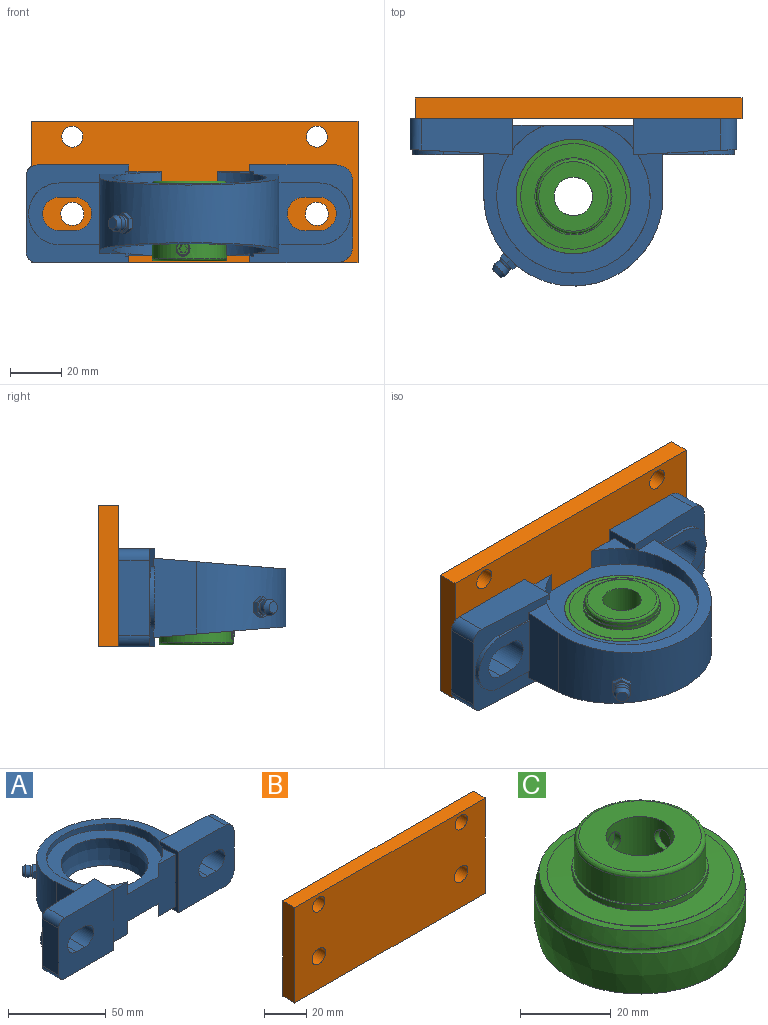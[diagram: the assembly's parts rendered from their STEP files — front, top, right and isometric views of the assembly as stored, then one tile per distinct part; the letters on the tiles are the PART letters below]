
ASSEMBLY  parts=3 mates=2
PART A: 64 faces, bbox 127x65x38 mm
  f0: plane 47x32.59mm, normal (0,-1,0), area 1189.2mm2, adj f1,f23,f24,f27,f29,f30,f32,f33
  f1: plane 38x14mm, normal (-1,0,0), area 163.5mm2, adj f0,f7,f24,f25,f29,f34,f35,f48
  f2: cylinder r=34.8mm len=69.6mm, axis (0,0,-1), area 2648.8mm2, adj f3,f4,f22,f28,f55
  f3: plane 30.82x16.77mm, normal (1,0,0), area 480.2mm2, adj f2,f8,f11,f12,f22,f25,f28
  f4: plane 30.82x16.77mm, normal (-1,0,0), area 480.2mm2, adj f2,f15,f18,f19,f22,f26,f28
  f5: plane 35.67x14mm, normal (0,0,1), area 467.5mm2, adj f26,f27,f47,f54
  f6: plane 35.67x14mm, normal (0,0,-1), area 467.5mm2, adj f26,f27,f47,f51
  f7: plane 33.5x14mm, normal (0,0,-1), area 440.9mm2, adj f1,f25,f50,f52
  f8: plane 15.7x1.35mm, normal (0,0,-1), area 15mm2, adj f3,f12,f25,f63
  f9: plane 14x6mm, normal (0,0,-1), area 84mm2, adj f10,f12,f14,f50
  f10: cylinder r=6.5mm len=14mm, axis (0,-1,0), area 285.9mm2, adj f9,f12,f13,f50
  f11: plane 15.7x1.35mm, normal (0,0,1), area 15mm2, adj f3,f12,f25,f63
  f12: plane 27.7x24mm, normal (0,1,0), area 392.3mm2, adj f3,f8,f9,f10,f11,f13,f14,f63
  f13: plane 14x6mm, normal (0,0,1), area 84mm2, adj f10,f12,f14,f50
  f14: cylinder r=6.5mm len=14mm, axis (0,-1,0), area 285.9mm2, adj f9,f12,f13,f50
  f15: plane 15.7x1.35mm, normal (0,0,1), area 15mm2, adj f4,f19,f26,f62
  f16: plane 14x6mm, normal (0,0,-1), area 84mm2, adj f17,f19,f21,f47
  f17: cylinder r=6.5mm len=14mm, axis (0,-1,0), area 285.9mm2, adj f16,f19,f20,f47
  f18: plane 15.7x1.35mm, normal (0,0,-1), area 15mm2, adj f4,f19,f26,f62
  f19: plane 27.7x24mm, normal (0,1,0), area 392.3mm2, adj f4,f15,f16,f17,f18,f20,f21,f62
  f20: plane 14x6mm, normal (0,0,1), area 84mm2, adj f17,f19,f21,f47
  f21: cylinder r=6.5mm len=14mm, axis (0,-1,0), area 285.9mm2, adj f16,f19,f20,f47
  f22: plane 69.6x54.55mm, normal (0,0.08,1), area 728.5mm2, adj f2,f3,f4,f25,f26,f61
  f23: plane 13.31x10.18mm, normal (0,0.08,1), area 47.9mm2, adj f0,f27,f61
  f24: plane 13.31x10.18mm, normal (0,0.08,1), area 47.9mm2, adj f0,f1,f61
  f25: plane 40x38mm, normal (0.05,1,0), area 548.5mm2, adj f1,f3,f7,f8,f11,f22,f28,f34
  f26: plane 40x38mm, normal (-0.05,1,0), area 558.1mm2, adj f4,f5,f6,f15,f18,f22,f27,f28
  f27: plane 38x14mm, normal (1,0,0), area 163.5mm2, adj f0,f5,f6,f23,f26,f30,f31,f36
  f28: plane 69.6x54.55mm, normal (0,0.08,-1), area 726.9mm2, adj f2,f3,f4,f25,f26,f60
  f29: plane 13.31x10.18mm, normal (0,0.08,-1), area 47.9mm2, adj f0,f1,f60
  f30: plane 13.31x10.18mm, normal (0,0.08,-1), area 47.9mm2, adj f0,f27,f60
  f31: plane 2.12x1.46mm, normal (0,0,-1), area 1.6mm2, adj f26,f27,f61
  f32: plane 59.6x57.5mm, normal (0,0,1), area 1200.7mm2, adj f0,f59,f61
  f33: plane 59.6x57.5mm, normal (0,0,-1), area 1200.7mm2, adj f0,f59,f60
  f34: plane 2.12x1.46mm, normal (0,0,1), area 1.6mm2, adj f1,f25,f60
  f35: plane 2.12x1.46mm, normal (0,0,-1), area 1.6mm2, adj f1,f25,f61
  f36: plane 2.12x1.46mm, normal (0,0,1), area 1.6mm2, adj f26,f27,f60
  f37: plane 4.5x3.18mm, normal (-0.71,0.71,0), area 15.9mm2, adj f58
  f38: plane 8.08x4.95mm, normal (-0.71,0.71,0), area 14.2mm2, adj f40,f41,f42,f43,f44,f45,f56
  f39: plane 8.08x4.95mm, normal (0.71,-0.71,0), area 14.2mm2, adj f40,f41,f42,f43,f44,f45,f55
  f40: plane 3.89x3.89mm, normal (-0.35,-0.35,0.87), area 8.1mm2, adj f38,f39,f41,f45
  f41: plane 4.04x1.41mm, normal (-0.71,-0.71,0), area 8.1mm2, adj f38,f39,f40,f42
  f42: plane 3.89x3.89mm, normal (-0.35,-0.35,-0.87), area 8.1mm2, adj f38,f39,f41,f43
  f43: plane 3.89x3.89mm, normal (0.35,0.35,-0.87), area 8.1mm2, adj f38,f39,f42,f44
  f44: plane 4.04x1.41mm, normal (0.71,0.71,0), area 8.1mm2, adj f38,f39,f43,f45
  f45: plane 3.89x3.89mm, normal (0.35,0.35,0.87), area 8.1mm2, adj f38,f39,f40,f44
  f46: plane 29.33x12mm, normal (-1,0,0), area 352mm2, adj f26,f47,f51,f54
  f47: plane 40x38mm, normal (0,-1,0), area 1301.2mm2, adj f5,f6,f16,f17,f20,f21,f27,f46
  f48: plane 33.5x14mm, normal (0,0,1), area 440.9mm2, adj f1,f25,f50,f53
  f49: plane 25x12mm, normal (1,0,0), area 300mm2, adj f25,f50,f52,f53
  f50: plane 40x38mm, normal (0,-1,0), area 1291.1mm2, adj f1,f7,f9,f10,f13,f14,f48,f49
  f51: cylinder r=4.33mm len=12.22mm, axis (0,1,0), area 82.2mm2, adj f6,f26,f46,f47
  f52: cylinder r=6.5mm len=12.33mm, axis (0,1,0), area 123.7mm2, adj f7,f25,f49,f50
  f53: cylinder r=6.5mm len=12.33mm, axis (0,1,0), area 123.7mm2, adj f25,f48,f49,f50
  f54: cylinder r=4.33mm len=12.22mm, axis (0,1,0), area 82.2mm2, adj f5,f26,f46,f47
  f55: cylinder r=3mm len=6mm, axis (-0.71,0.71,0), area 1.4mm2, adj f2,f39
  f56: revolved ~6x4.77mm, area 18.6mm2, adj f38,f57
  f57: revolved ~6.5x6.01mm, area 48.1mm2, adj f56,f58
  f58: revolved ~6.5x5.3mm, area 38.6mm2, adj f37,f57
  f59: revolved ~47x47mm, area 2500.5mm2, adj f32,f33
  f60: cylinder r=29.8mm len=59.6mm, axis (0,0,1), area 865.4mm2, adj f0,f1,f25,f26,f27,f28,f29,f30
  f61: cylinder r=29.8mm len=59.6mm, axis (0,0,1), area 865.4mm2, adj f0,f1,f22,f23,f24,f25,f26,f27
  f62: cylinder r=12mm len=24mm, axis (0,-1,0), area 65.3mm2, adj f15,f18,f19,f26
  f63: cylinder r=12mm len=24mm, axis (0,-1,0), area 65.3mm2, adj f8,f11,f12,f25
PART B: 10 faces, bbox 127x8x55 mm
  f0: plane 127x8mm, normal (0,0,1), area 1016mm2, adj f1,f3,f4,f5
  f1: plane 55x8mm, normal (-1,0,0), area 440mm2, adj f0,f2,f4,f5
  f2: plane 127x8mm, normal (0,0,-1), area 1016mm2, adj f1,f3,f4,f5
  f3: plane 55x8mm, normal (1,0,0), area 440mm2, adj f0,f2,f4,f5
  f4: plane 127x55mm, normal (0,-1,0), area 6752.1mm2, adj f0,f1,f2,f3,f6,f7,f8,f9
  f5: plane 127x55mm, normal (0,1,0), area 6752.1mm2, adj f0,f1,f2,f3,f6,f7,f8,f9
  f6: cylinder r=4.5mm len=9mm, axis (0,-1,0), area 226.2mm2, adj f4,f5
  f7: cylinder r=4.5mm len=9mm, axis (0,-1,0), area 226.2mm2, adj f4,f5
  f8: cylinder r=4.1mm len=8.2mm, axis (0,-1,0), area 206.1mm2, adj f4,f5
  f9: cylinder r=4.1mm len=8.2mm, axis (0,-1,0), area 206.1mm2, adj f4,f5
PART C: 46 faces, bbox 47x47x31 mm
  f0: plane 27x27mm, normal (0,0,1), area 395.8mm2, adj f1,f39
  f1: revolved ~29x29mm, area 139.5mm2, adj f0,f2
  f2: cylinder r=14.5mm len=29mm, axis (0,0,1), area 590.5mm2, adj f1,f3,f13,f29
  f3: revolved ~6x5.91mm, area 4.3mm2, adj f2,f4
  f4: revolved ~5.39x5.3mm, area 6.9mm2, adj f3,f5
  f5: plane 4.77x4.7mm, normal (-0.17,0.98,0), area 10.1mm2, adj f4,f6,f8,f9,f10,f11,f12
  f6: plane 3.11x1.5mm, normal (0.85,0.15,-0.5), area 5.2mm2, adj f5,f7,f8,f12
  f7: plane 3.41x3mm, normal (-0.17,0.98,0), area 7.8mm2, adj f6,f8,f9,f10,f11,f12
  f8: plane 3.26x2.23mm, normal (0,0,-1), area 5.2mm2, adj f5,f6,f7,f9
  f9: plane 3.11x1.5mm, normal (-0.85,-0.15,-0.5), area 5.2mm2, adj f5,f7,f8,f10
  f10: plane 3.11x1.5mm, normal (-0.85,-0.15,0.5), area 5.2mm2, adj f5,f7,f9,f11
  f11: plane 3.26x2.23mm, normal (0,0,1), area 5.2mm2, adj f5,f7,f10,f12
  f12: plane 3.11x1.5mm, normal (0.85,0.15,0.5), area 5.2mm2, adj f5,f6,f7,f11
  f13: plane 30x30mm, normal (0,0,1), area 46.3mm2, adj f2,f14
  f14: cylinder r=15mm len=30mm, axis (0,0,1), area 136.7mm2, adj f13,f15
  f15: revolved ~41x41mm, area 613.8mm2, adj f14,f16
  f16: cylinder r=20.5mm len=41mm, axis (0,0,1), area 12.9mm2, adj f15,f17
  f17: plane 44.54x44.54mm, normal (0,0,1), area 237.9mm2, adj f16,f18
  f18: revolved ~46.34x46.34mm, area 595.4mm2, adj f17,f19
  f19: revolved ~46.69x46.69mm, area 263.6mm2, adj f18,f20
  f20: revolved ~47x47mm, area 1699.3mm2, adj f19,f21
  f21: plane 44.54x44.54mm, normal (0,0,-1), area 237.9mm2, adj f20,f22
  f22: cylinder r=20.5mm len=41mm, axis (0,0,1), area 12.9mm2, adj f21,f23
  f23: revolved ~41x41mm, area 613.8mm2, adj f22,f24
  f24: cylinder r=15mm len=30mm, axis (0,0,1), area 136.7mm2, adj f23,f25
  f25: plane 30x30mm, normal (0,0,-1), area 46.3mm2, adj f24,f26
  f26: cylinder r=14.5mm len=29mm, axis (0,0,1), area 132.1mm2, adj f25,f27
  f27: revolved ~29x29mm, area 139.5mm2, adj f26,f28
  f28: plane 27x27mm, normal (0,0,-1), area 395.8mm2, adj f27,f39
  f29: revolved ~6x6mm, area 4.3mm2, adj f2,f30
  f30: revolved ~5.39x5.39mm, area 6.9mm2, adj f29,f31
  f31: plane 4.77x4.77mm, normal (1,0,0), area 10.1mm2, adj f30,f32,f34,f35,f36,f37,f38
  f32: plane 3x1.5mm, normal (0,-0.87,-0.5), area 5.2mm2, adj f31,f33,f34,f38
  f33: plane 3.46x3mm, normal (1,0,0), area 7.8mm2, adj f32,f34,f35,f36,f37,f38
  f34: plane 3x1.73mm, normal (0,0,-1), area 5.2mm2, adj f31,f32,f33,f35
  f35: plane 3x1.5mm, normal (0,0.87,-0.5), area 5.2mm2, adj f31,f33,f34,f36
  f36: plane 3x1.5mm, normal (0,0.87,0.5), area 5.2mm2, adj f31,f33,f35,f37
  f37: plane 3x1.73mm, normal (0,0,1), area 5.2mm2, adj f31,f33,f36,f38
  f38: plane 3x1.5mm, normal (0,-0.87,0.5), area 5.2mm2, adj f31,f32,f33,f37
  f39: cylinder r=7.5mm len=31mm, axis (0,0,1), area 1417.9mm2, adj f0,f28,f40,f43
  f40: cylinder r=2.59mm len=5.4mm, axis (0.17,-0.98,0), area 23.4mm2, adj f39,f41
  f41: revolved ~5.19x5.11mm, area 0mm2, adj f40,f42
  f42: plane 4.77x4.7mm, normal (0.17,-0.98,0), area 17.9mm2, adj f41
  f43: cylinder r=2.59mm len=5.19mm, axis (-1,0,0), area 23.4mm2, adj f39,f44
  f44: revolved ~5.19x5.19mm, area 4.6mm2, adj f43,f45
  f45: plane 4.77x4.77mm, normal (-1,0,0), area 17.9mm2, adj f44
PLACE A rot(axis=(1,0,0),180deg) t=(10.13,-16.31,-59.24)mm
PLACE B t=(13.3,-8.31,-198.33)mm fixed
PLACE C rot(axis=(1,0,0),180deg) t=(10.13,-16.31,-59.24)mm
MATE pin_slot B.f6 <-> A.f62  axis (0,-1,0) through (-35.37,-16.31,-59.24)mm
MATE planar A.f5 <-> B.f2  axis (0,0,-1) through (-30.8,-22.87,-78.24)mm
